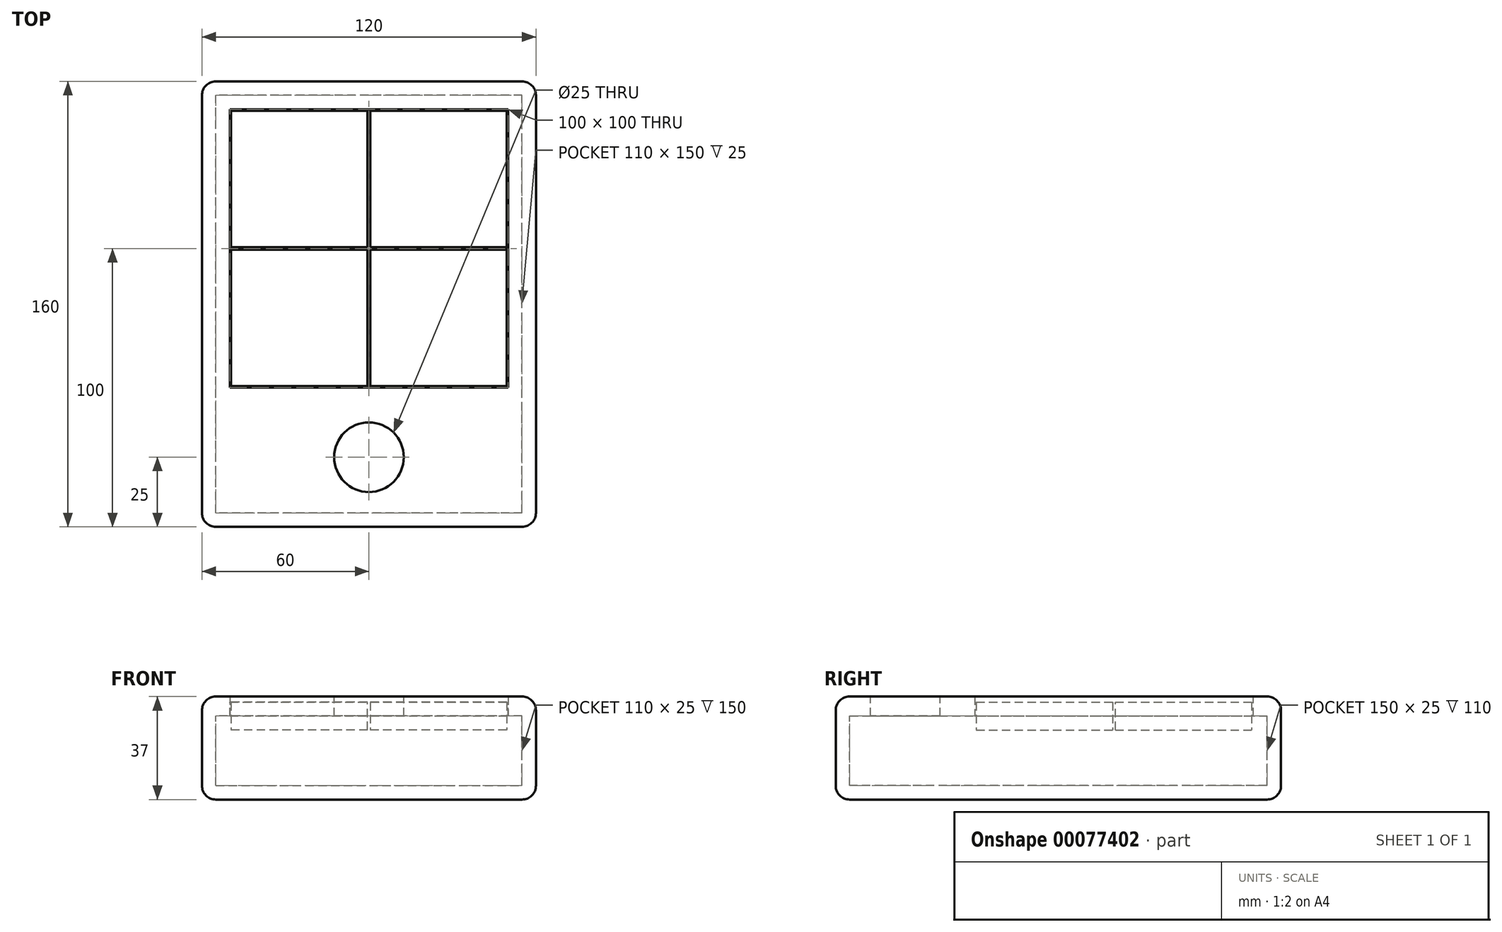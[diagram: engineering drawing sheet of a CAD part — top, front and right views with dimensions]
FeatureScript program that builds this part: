
annotation { "Feature Type Name" : "Feature", "Feature Type Description" : "" }
export const myFeature = defineFeature(function(context is Context, id is Id, definition is map)
    precondition{}
    {
        {
            var Q0;
            Q0=qCreatedBy(makeId("Top.planeOp"),FACE);
            var sketch = newSketch(context, id + "F0", { "sketchPlane" : qUnion([Q0])});
            skLineSegment(sketch, "E0.bottom", {"start": v(-50, 50) * mm, "end": v(50, 50) * mm});
            skLineSegment(sketch, "E0.top", {"start": v(-50, -50) * mm, "end": v(50, -50) * mm});
            skLineSegment(sketch, "E0.left", {"start": v(-50, 50) * mm, "end": v(-50, -50) * mm});
            skLineSegment(sketch, "E0.right", {"start": v(50, 50) * mm, "end": v(50, -50) * mm});
            skPoint(sketch, "E0.middle", {"position": v(0, 0) * mm});
            skSolve(sketch);
        }
        {
            var Q0;
            Q0=makeQuery(id+"F0.imprint","IMPRINT",FACE,{"disambiguationData":[TD([[makeQuery(id+"F0.imprint","IMPRINT",EDGE,{"derivedFrom":sQuery(id+"F0.wireOp",EDGE,"E0.bottom")}),-1.0]])]});
            extrude(context, id + "F1", {"entities" : qUnion([Q0]), "depth" : 10 * mm});
        }
        {
            var Q0;
            Q0=makeQuery(id+"F1.opExtrude","SWEPT_FACE",FACE,{"disambiguationData":[OSD([sQuery(id+"F0.wireOp",EDGE,"E0.top")])]});
            var sketch = newSketch(context, id + "F2", { "sketchPlane" : qUnion([Q0])});
            skLineSegment(sketch, "E1.bottom", {"start": v(-50, 10) * mm, "end": v(50, 10) * mm});
            skLineSegment(sketch, "E1.top", {"start": v(-50, 5) * mm, "end": v(50, 5) * mm});
            skLineSegment(sketch, "E1.left", {"start": v(-50, 10) * mm, "end": v(-50, 5) * mm});
            skLineSegment(sketch, "E1.right", {"start": v(50, 10) * mm, "end": v(50, 5) * mm});
            skSolve(sketch);
        }
        {
            var Q0;
            Q0=makeQuery(id+"F2.imprint","IMPRINT",FACE,{"disambiguationData":[TD([[makeQuery(id+"F2.imprint","IMPRINT",EDGE,{"derivedFrom":sQuery(id+"F2.wireOp",EDGE,"E1.bottom")}),-1.0]])]});
            extrude(context, id + "F3", {"entities" : qUnion([Q0]), "operationType" : NewBodyOperationType.ADD, "depth" : 50 * mm});
        }
        {
            var Q0;
            Q0=makeQuery(id+"F3.boolean.opBoolean","MERGE",FACE,{"derivedFrom":[makeQuery(id+"F1.opExtrude","CAP_FACE",FACE,{"disambiguationData":[OSD([sQuery(id+"F0.wireOp",EDGE,"E0.bottom"),sQuery(id+"F0.wireOp",EDGE,"E0.top"),sQuery(id+"F0.wireOp",EDGE,"E0.left"),sQuery(id+"F0.wireOp",EDGE,"E0.right")])],"isStart":false}),makeQuery(id+"F3.opExtrude","SWEPT_FACE",FACE,{"disambiguationData":[OSD([sQuery(id+"F2.wireOp",EDGE,"E1.bottom")])]})]});
            var sketch = newSketch(context, id + "F4", { "sketchPlane" : qUnion([Q0])});
            skLineSegment(sketch, "E2.bottom", {"start": v(-50, -100) * mm, "end": v(50, -100) * mm});
            skLineSegment(sketch, "E2.top", {"start": v(-50, -50) * mm, "end": v(50, -50) * mm});
            skLineSegment(sketch, "E2.left", {"start": v(-50, -100) * mm, "end": v(-50, -50) * mm});
            skLineSegment(sketch, "E2.right", {"start": v(50, -100) * mm, "end": v(50, -50) * mm});
            skSolve(sketch);
        }
        {
            var Q0;
            Q0=makeQuery(id+"F4.imprint","IMPRINT",FACE,{"disambiguationData":[TD([[makeQuery(id+"F4.imprint","IMPRINT",EDGE,{"derivedFrom":sQuery(id+"F4.wireOp",EDGE,"E2.bottom")}),1.0]])]});
            extrude(context, id + "F5", {"entities" : qUnion([Q0]), "operationType" : NewBodyOperationType.ADD, "depth" : 2 * mm});
        }
        {
            var Q0;
            Q0=makeQuery(id+"F5.boolean.opBoolean","MERGE",FACE,{"derivedFrom":[makeQuery(id+"F3.boolean.opBoolean","MERGE",FACE,{"derivedFrom":[makeQuery(id+"F1.opExtrude","SWEPT_FACE",FACE,{"disambiguationData":[OSD([sQuery(id+"F0.wireOp",EDGE,"E0.right")])]}),makeQuery(id+"F3.opExtrude","SWEPT_FACE",FACE,{"disambiguationData":[OSD([sQuery(id+"F2.wireOp",EDGE,"E1.right")])]})]}),makeQuery(id+"F5.opExtrude","SWEPT_FACE",FACE,{"disambiguationData":[OSD([sQuery(id+"F4.wireOp",EDGE,"E2.right")])]})]});
            var sketch = newSketch(context, id + "F6", { "sketchPlane" : qUnion([Q0])});
            skLineSegment(sketch, "E3", {"start": v(-50, 5) * mm, "end": v(50, 5) * mm});
            skSolve(sketch);
        }
        {
            var Q0;
            {var subQ4=sQuery(id+"F6.wireOp",EDGE,"E3");Q0=makeQuery(id+"F6.imprint","IMPRINT",FACE,{"disambiguationData":[TD([[makeQuery(id+"F6.imprint","IMPRINT",EDGE,{"derivedFrom":subQ4}),1.0]])]});}
            extrude(context, id + "F7", {"entities" : qUnion([Q0]), "operationType" : NewBodyOperationType.ADD, "depth" : 10 * mm});
        }
        {
            var Q0;
            {var subQ0=sQuery(id+"F2.wireOp",EDGE,"E1.bottom");var subQ1=sQuery(id+"F0.wireOp",EDGE,"E0.right");Q0=makeQuery(id+"F7.boolean.opBoolean","MERGE",FACE,{"derivedFrom":[makeQuery(id+"F3.boolean.opBoolean","MERGE",FACE,{"derivedFrom":[makeQuery(id+"F1.opExtrude","CAP_FACE",FACE,{"disambiguationData":[OSD([sQuery(id+"F0.wireOp",EDGE,"E0.bottom"),sQuery(id+"F0.wireOp",EDGE,"E0.top"),sQuery(id+"F0.wireOp",EDGE,"E0.left"),subQ1])],"isStart":false}),makeQuery(id+"F3.opExtrude","SWEPT_FACE",FACE,{"disambiguationData":[OSD([subQ0])]})]}),makeQuery(id+"F7.opExtrude","SWEPT_FACE",FACE,{"disambiguationData":[OSD([subQ1,subQ0,sQuery(id+"F2.wireOp",EDGE,"E1.right")])]})]});}
            var sketch = newSketch(context, id + "F8", { "sketchPlane" : qUnion([Q0])});
            skLineSegment(sketch, "E4.bottom", {"start": v(60, 50) * mm, "end": v(50, 50) * mm});
            skLineSegment(sketch, "E4.top", {"start": v(60, -50) * mm, "end": v(50, -50) * mm});
            skLineSegment(sketch, "E4.left", {"start": v(60, 50) * mm, "end": v(60, -50) * mm});
            skLineSegment(sketch, "E4.right", {"start": v(50, 50) * mm, "end": v(50, -50) * mm});
            skSolve(sketch);
        }
        {
            var Q0;
            Q0=makeQuery(id+"F8.imprint","IMPRINT",FACE,{"disambiguationData":[TD([[makeQuery(id+"F8.imprint","IMPRINT",EDGE,{"derivedFrom":sQuery(id+"F8.wireOp",EDGE,"E4.bottom")}),-1.0]])]});
            extrude(context, id + "F9", {"entities" : qUnion([Q0]), "operationType" : NewBodyOperationType.ADD, "depth" : 2 * mm});
        }
        {
            var Q0;
            {var subQ0=sQuery(id+"F0.wireOp",EDGE,"E0.bottom");Q0=makeQuery(id+"F9.boolean.opBoolean","MERGE",FACE,{"derivedFrom":[makeQuery(id+"F7.boolean.opBoolean","MERGE",FACE,{"derivedFrom":[makeQuery(id+"F1.opExtrude","SWEPT_FACE",FACE,{"disambiguationData":[OSD([subQ0])]}),makeQuery(id+"F7.opExtrude","SWEPT_FACE",FACE,{"disambiguationData":[OSD([subQ0,sQuery(id+"F0.wireOp",EDGE,"E0.right")])]})]}),makeQuery(id+"F9.opExtrude","SWEPT_FACE",FACE,{"disambiguationData":[OSD([sQuery(id+"F8.wireOp",EDGE,"E4.bottom")])]})]});}
            var sketch = newSketch(context, id + "F10", { "sketchPlane" : qUnion([Q0])});
            skLineSegment(sketch, "E5", {"start": v(-50, 5) * mm, "end": v(50, 5) * mm});
            skSolve(sketch);
        }
        {
            var Q0;
            {var subQ5=sQuery(id+"F10.wireOp",EDGE,"E5");Q0=makeQuery(id+"F10.imprint","IMPRINT",FACE,{"disambiguationData":[TD([[makeQuery(id+"F10.imprint","IMPRINT",EDGE,{"derivedFrom":subQ5}),1.0]])]});}
            extrude(context, id + "F11", {"entities" : qUnion([Q0]), "operationType" : NewBodyOperationType.ADD, "depth" : 10 * mm});
        }
        {
            var Q0;
            {var subQ0=sQuery(id+"F2.wireOp",EDGE,"E1.right");var subQ1=sQuery(id+"F2.wireOp",EDGE,"E1.bottom");var subQ2=sQuery(id+"F0.wireOp",EDGE,"E0.right");var subQ3=sQuery(id+"F0.wireOp",EDGE,"E0.bottom");Q0=makeQuery(id+"F11.boolean.opBoolean","MERGE",FACE,{"derivedFrom":[makeQuery(id+"F7.boolean.opBoolean","MERGE",FACE,{"derivedFrom":[makeQuery(id+"F3.boolean.opBoolean","MERGE",FACE,{"derivedFrom":[makeQuery(id+"F1.opExtrude","CAP_FACE",FACE,{"disambiguationData":[OSD([subQ3,sQuery(id+"F0.wireOp",EDGE,"E0.top"),sQuery(id+"F0.wireOp",EDGE,"E0.left"),subQ2])],"isStart":false}),makeQuery(id+"F3.opExtrude","SWEPT_FACE",FACE,{"disambiguationData":[OSD([subQ1])]})]}),makeQuery(id+"F7.opExtrude","SWEPT_FACE",FACE,{"disambiguationData":[OSD([subQ2,subQ1,subQ0])]})]}),makeQuery(id+"F11.opExtrude","SWEPT_FACE",FACE,{"disambiguationData":[OSD([subQ3,subQ2,subQ1,subQ0])]})]});}
            var sketch = newSketch(context, id + "F12", { "sketchPlane" : qUnion([Q0])});
            skLineSegment(sketch, "E6.bottom", {"start": v(-50, 60) * mm, "end": v(50, 60) * mm});
            skLineSegment(sketch, "E6.top", {"start": v(-50, 49.98) * mm, "end": v(50, 49.98) * mm});
            skLineSegment(sketch, "E6.left", {"start": v(-50, 60) * mm, "end": v(-50, 49.98) * mm});
            skLineSegment(sketch, "E6.right", {"start": v(50, 60) * mm, "end": v(50, 49.98) * mm});
            skSolve(sketch);
        }
        {
            var Q0;
            Q0 = qSketchRegion(id + "F12", true);
            extrude(context, id + "F13", {"entities" : qUnion([Q0]), "operationType" : NewBodyOperationType.ADD, "depth" : 2 * mm});
        }
        {
            var Q0;
            {var subQ0=sQuery(id+"F0.wireOp",EDGE,"E0.left");Q0=makeQuery(id+"F13.boolean.opBoolean","MERGE",FACE,{"derivedFrom":[makeQuery(id+"F11.boolean.opBoolean","MERGE",FACE,{"derivedFrom":[makeQuery(id+"F5.boolean.opBoolean","MERGE",FACE,{"derivedFrom":[makeQuery(id+"F3.boolean.opBoolean","MERGE",FACE,{"derivedFrom":[makeQuery(id+"F1.opExtrude","SWEPT_FACE",FACE,{"disambiguationData":[OSD([subQ0])]}),makeQuery(id+"F3.opExtrude","SWEPT_FACE",FACE,{"disambiguationData":[OSD([sQuery(id+"F2.wireOp",EDGE,"E1.left")])]})]}),makeQuery(id+"F5.opExtrude","SWEPT_FACE",FACE,{"disambiguationData":[OSD([sQuery(id+"F4.wireOp",EDGE,"E2.left")])]})]}),makeQuery(id+"F11.opExtrude","SWEPT_FACE",FACE,{"disambiguationData":[OSD([sQuery(id+"F0.wireOp",EDGE,"E0.bottom"),subQ0])]})]}),makeQuery(id+"F13.opExtrude","SWEPT_FACE",FACE,{"disambiguationData":[OSD([sQuery(id+"F12.wireOp",EDGE,"E6.left")])]})]});}
            var sketch = newSketch(context, id + "F14", { "sketchPlane" : qUnion([Q0])});
            skSolve(sketch);
        }
        {
            var Q0;
            Q0 = qSketchRegion(id + "F14", true);
            var Q1;
            {var subQ5=sQuery(id+"F0.wireOp",EDGE,"E0.left");Q1=makeQuery(id+"F14.imprint","IMPRINT",FACE,{"disambiguationData":[TD([[makeQuery(id+"F14.imprint","IMPRINT",EDGE,{"derivedFrom":makeQuery(id+"F1.opExtrude","CAP_EDGE",EDGE,{"disambiguationData":[OSD([subQ5])],"isStart":true})}),1.0]])]});}
            extrude(context, id + "F15", {"entities" : qUnion([Q0, Q1]), "operationType" : NewBodyOperationType.ADD, "depth" : 10 * mm});
        }
        {
            var Q0;
            {var subQ0=sQuery(id+"F2.wireOp",EDGE,"E1.right");var subQ1=sQuery(id+"F2.wireOp",EDGE,"E1.bottom");var subQ2=sQuery(id+"F0.wireOp",EDGE,"E0.right");var subQ3=sQuery(id+"F0.wireOp",EDGE,"E0.left");var subQ4=sQuery(id+"F0.wireOp",EDGE,"E0.bottom");Q0=makeQuery(id+"F15.boolean.opBoolean","MERGE",FACE,{"derivedFrom":[makeQuery(id+"F11.boolean.opBoolean","MERGE",FACE,{"derivedFrom":[makeQuery(id+"F7.boolean.opBoolean","MERGE",FACE,{"derivedFrom":[makeQuery(id+"F3.boolean.opBoolean","MERGE",FACE,{"derivedFrom":[makeQuery(id+"F1.opExtrude","CAP_FACE",FACE,{"disambiguationData":[OSD([subQ4,sQuery(id+"F0.wireOp",EDGE,"E0.top"),subQ3,subQ2])],"isStart":false}),makeQuery(id+"F3.opExtrude","SWEPT_FACE",FACE,{"disambiguationData":[OSD([subQ1])]})]}),makeQuery(id+"F7.opExtrude","SWEPT_FACE",FACE,{"disambiguationData":[OSD([subQ2,subQ1,subQ0])]})]}),makeQuery(id+"F11.opExtrude","SWEPT_FACE",FACE,{"disambiguationData":[OSD([subQ4,subQ2,subQ1,subQ0])]})]}),makeQuery(id+"F15.opExtrude","SWEPT_FACE",FACE,{"disambiguationData":[OSD([subQ4,subQ3,subQ2,subQ1,sQuery(id+"F2.wireOp",EDGE,"E1.left"),subQ0])]})]});}
            var sketch = newSketch(context, id + "F16", { "sketchPlane" : qUnion([Q0])});
            skLineSegment(sketch, "E7.bottom", {"start": v(-60, 49.98) * mm, "end": v(-50, 49.98) * mm});
            skLineSegment(sketch, "E7.top", {"start": v(-60, -50) * mm, "end": v(-50, -50) * mm});
            skLineSegment(sketch, "E7.left", {"start": v(-60, 49.98) * mm, "end": v(-60, -50) * mm});
            skLineSegment(sketch, "E7.right", {"start": v(-50, 49.98) * mm, "end": v(-50, -50) * mm});
            skSolve(sketch);
        }
        {
            var Q0;
            Q0 = qSketchRegion(id + "F16", true);
            extrude(context, id + "F17", {"entities" : qUnion([Q0]), "operationType" : NewBodyOperationType.ADD, "depth" : 2 * mm});
        }
        {
            var Q0;
            {var subQ0=sQuery(id+"F2.wireOp",EDGE,"E1.right");var subQ1=sQuery(id+"F2.wireOp",EDGE,"E1.bottom");var subQ2=sQuery(id+"F0.wireOp",EDGE,"E0.right");var subQ3=sQuery(id+"F0.wireOp",EDGE,"E0.left");var subQ4=sQuery(id+"F0.wireOp",EDGE,"E0.bottom");Q0=makeQuery(id+"F15.boolean.opBoolean","MERGE",FACE,{"derivedFrom":[makeQuery(id+"F11.boolean.opBoolean","MERGE",FACE,{"derivedFrom":[makeQuery(id+"F7.boolean.opBoolean","MERGE",FACE,{"derivedFrom":[makeQuery(id+"F3.boolean.opBoolean","MERGE",FACE,{"derivedFrom":[makeQuery(id+"F1.opExtrude","CAP_FACE",FACE,{"disambiguationData":[OSD([subQ4,sQuery(id+"F0.wireOp",EDGE,"E0.top"),subQ3,subQ2])],"isStart":false}),makeQuery(id+"F3.opExtrude","SWEPT_FACE",FACE,{"disambiguationData":[OSD([subQ1])]})]}),makeQuery(id+"F7.opExtrude","SWEPT_FACE",FACE,{"disambiguationData":[OSD([subQ2,subQ1,subQ0])]})]}),makeQuery(id+"F11.opExtrude","SWEPT_FACE",FACE,{"disambiguationData":[OSD([subQ4,subQ2,subQ1,subQ0])]})]}),makeQuery(id+"F15.opExtrude","SWEPT_FACE",FACE,{"disambiguationData":[OSD([subQ4,subQ3,subQ2,subQ1,sQuery(id+"F2.wireOp",EDGE,"E1.left"),subQ0])]})]});}
            var sketch = newSketch(context, id + "F18", { "sketchPlane" : qUnion([Q0])});
            skLineSegment(sketch, "E8.bottom", {"start": v(0.5, -50) * mm, "end": v(-0.5, -50) * mm});
            skLineSegment(sketch, "E8.left", {"start": v(0.5, -50) * mm, "end": v(0.5, -0.5) * mm});
            skLineSegment(sketch, "E8.right", {"start": v(-0.5, -50) * mm, "end": v(-0.5, -0.5) * mm});
            skLineSegment(sketch, "E9.bottom", {"start": v(-0.5, -0.5) * mm, "end": v(-50, -0.5) * mm});
            skLineSegment(sketch, "E9.top", {"start": v(-0.5, 0.48) * mm, "end": v(-50, 0.48) * mm});
            skLineSegment(sketch, "E9.right", {"start": v(-50, -0.5) * mm, "end": v(-50, 0.48) * mm});
            skLineSegment(sketch, "E10.top", {"start": v(0.5, 49.98) * mm, "end": v(-0.5, 49.98) * mm});
            skLineSegment(sketch, "E10.left", {"start": v(0.5, 0.48) * mm, "end": v(0.5, 49.98) * mm});
            skLineSegment(sketch, "E10.right", {"start": v(-0.5, 0.48) * mm, "end": v(-0.5, 49.98) * mm});
            skLineSegment(sketch, "E11.bottom", {"start": v(50, -0.5) * mm, "end": v(0.5, -0.5) * mm});
            skLineSegment(sketch, "E11.top", {"start": v(50, 0.48) * mm, "end": v(0.5, 0.48) * mm});
            skLineSegment(sketch, "E11.left", {"start": v(50, -0.5) * mm, "end": v(50, 0.48) * mm});
            skSolve(sketch);
        }
        {
            var Q0;
            Q0 = qSketchRegion(id + "F18", true);
            extrude(context, id + "F19", {"entities" : qUnion([Q0]), "operationType" : NewBodyOperationType.REMOVE, "oppositeDirection" : true, "depth" : 10 * mm});
        }
        {
            var Q0;
            {var subQ0=sQuery(id+"F0.wireOp",EDGE,"E0.left");Q0=makeQuery(id+"F15.boolean.opBoolean","MERGE",FACE,{"derivedFrom":[makeQuery(id+"F1.opExtrude","CAP_FACE",FACE,{"disambiguationData":[OSD([sQuery(id+"F0.wireOp",EDGE,"E0.bottom"),sQuery(id+"F0.wireOp",EDGE,"E0.top"),subQ0,sQuery(id+"F0.wireOp",EDGE,"E0.right")])],"isStart":true}),makeQuery(id+"F15.opExtrude","SWEPT_FACE",FACE,{"disambiguationData":[OSD([subQ0])]})]});}
            var sketch = newSketch(context, id + "F20", { "sketchPlane" : qUnion([Q0])});
            skLineSegment(sketch, "E12.bottom", {"start": v(-60, 50) * mm, "end": v(-50, 50) * mm});
            skLineSegment(sketch, "E12.top", {"start": v(-60, -50) * mm, "end": v(-50, -50) * mm});
            skLineSegment(sketch, "E12.left", {"start": v(-60, 50) * mm, "end": v(-60, -50) * mm});
            skLineSegment(sketch, "E12.right", {"start": v(-50, 50) * mm, "end": v(-50, -50) * mm});
            skSolve(sketch);
        }
        {
            var Q0;
            Q0 = qSketchRegion(id + "F20", true);
            extrude(context, id + "F21", {"entities" : qUnion([Q0]), "operationType" : NewBodyOperationType.REMOVE, "oppositeDirection" : true, "depth" : 5 * mm});
        }
        {
            var Q0;
            {var subQ0=sQuery(id+"F12.wireOp",EDGE,"E6.left");var subQ1=sQuery(id+"F4.wireOp",EDGE,"E2.left");var subQ2=sQuery(id+"F8.wireOp",EDGE,"E4.bottom");var subQ3=sQuery(id+"F4.wireOp",EDGE,"E2.right");Q0=makeQuery(id+"F17.boolean.opBoolean","MERGE",FACE,{"derivedFrom":[makeQuery(id+"F15.boolean.opBoolean","MERGE",FACE,{"derivedFrom":[makeQuery(id+"F13.boolean.opBoolean","MERGE",FACE,{"derivedFrom":[makeQuery(id+"F11.boolean.opBoolean","MERGE",FACE,{"derivedFrom":[makeQuery(id+"F9.boolean.opBoolean","MERGE",FACE,{"derivedFrom":[makeQuery(id+"F7.boolean.opBoolean","MERGE",FACE,{"derivedFrom":[makeQuery(id+"F5.opExtrude","CAP_FACE",FACE,{"disambiguationData":[OSD([sQuery(id+"F4.wireOp",EDGE,"E2.bottom"),sQuery(id+"F4.wireOp",EDGE,"E2.top"),subQ1,subQ3])],"isStart":false}),makeQuery(id+"F7.opExtrude","SWEPT_FACE",FACE,{"disambiguationData":[OSD([subQ3])]})]}),makeQuery(id+"F9.opExtrude","CAP_FACE",FACE,{"disambiguationData":[OSD([subQ2,sQuery(id+"F8.wireOp",EDGE,"E4.top"),sQuery(id+"F8.wireOp",EDGE,"E4.left"),sQuery(id+"F8.wireOp",EDGE,"E4.right")])],"isStart":false})]}),makeQuery(id+"F11.opExtrude","SWEPT_FACE",FACE,{"disambiguationData":[OSD([subQ2])]})]}),makeQuery(id+"F13.opExtrude","CAP_FACE",FACE,{"disambiguationData":[OSD([sQuery(id+"F12.wireOp",EDGE,"E6.bottom"),sQuery(id+"F12.wireOp",EDGE,"E6.top"),subQ0,sQuery(id+"F12.wireOp",EDGE,"E6.right")])],"isStart":false})]}),makeQuery(id+"F15.opExtrude","SWEPT_FACE",FACE,{"disambiguationData":[OSD([subQ1])]}),makeQuery(id+"F15.opExtrude","SWEPT_FACE",FACE,{"disambiguationData":[OSD([subQ0])]})]}),makeQuery(id+"F17.opExtrude","CAP_FACE",FACE,{"disambiguationData":[OSD([sQuery(id+"F16.wireOp",EDGE,"E7.bottom"),sQuery(id+"F16.wireOp",EDGE,"E7.top"),sQuery(id+"F16.wireOp",EDGE,"E7.left"),sQuery(id+"F16.wireOp",EDGE,"E7.right")])],"isStart":false})]});}
            var sketch = newSketch(context, id + "F22", { "sketchPlane" : qUnion([Q0])});
            skCircle(sketch, "E13", {"center": v(0, -75) * mm, "radius": 12.5 * mm});
            skSolve(sketch);
        }
        {
            var Q0;
            Q0 = qSketchRegion(id + "F22", true);
            extrude(context, id + "F23", {"entities" : qUnion([Q0]), "operationType" : NewBodyOperationType.REMOVE, "oppositeDirection" : true, "depth" : 7 * mm});
        }
        {
            var Q0;
            {var subQ1=sQuery(id+"F2.wireOp",EDGE,"E1.left");var subQ2=sQuery(id+"F2.wireOp",EDGE,"E1.bottom");var subQ3=sQuery(id+"F0.wireOp",EDGE,"E0.left");var subQ4=sQuery(id+"F2.wireOp",EDGE,"E1.right");var subQ5=sQuery(id+"F0.wireOp",EDGE,"E0.right");var subQ6=sQuery(id+"F0.wireOp",EDGE,"E0.bottom");Q0=makeQuery(id+"F19.boolean.opBoolean","SPLIT",FACE,{"disambiguationData":[TD([makeQuery(id+"F19.opExtrude","SWEPT_FACE",FACE,{"disambiguationData":[OSD([sQuery(id+"F18.wireOp",EDGE,"E8.right")])]})])],"derivedFrom":makeQuery(id+"F15.boolean.opBoolean","MERGE",FACE,{"derivedFrom":[makeQuery(id+"F11.boolean.opBoolean","MERGE",FACE,{"derivedFrom":[makeQuery(id+"F7.boolean.opBoolean","MERGE",FACE,{"derivedFrom":[makeQuery(id+"F3.boolean.opBoolean","MERGE",FACE,{"derivedFrom":[makeQuery(id+"F1.opExtrude","CAP_FACE",FACE,{"disambiguationData":[OSD([subQ6,sQuery(id+"F0.wireOp",EDGE,"E0.top"),subQ3,subQ5])],"isStart":false}),makeQuery(id+"F3.opExtrude","SWEPT_FACE",FACE,{"disambiguationData":[OSD([subQ2])]})]}),makeQuery(id+"F7.opExtrude","SWEPT_FACE",FACE,{"disambiguationData":[OSD([subQ5,subQ2,subQ4])]})]}),makeQuery(id+"F11.opExtrude","SWEPT_FACE",FACE,{"disambiguationData":[OSD([subQ6,subQ5,subQ2,subQ4])]})]}),makeQuery(id+"F15.opExtrude","SWEPT_FACE",FACE,{"disambiguationData":[OSD([subQ6,subQ3,subQ5,subQ2,subQ1,subQ4])]})]})});}
            var sketch = newSketch(context, id + "F24", { "sketchPlane" : qUnion([Q0])});
            skLineSegment(sketch, "E14.bottom", {"start": v(-49.5, -49.5) * mm, "end": v(49.5, -49.5) * mm});
            skLineSegment(sketch, "E14.top", {"start": v(-49.5, 49.48) * mm, "end": v(49.5, 49.48) * mm});
            skLineSegment(sketch, "E14.left", {"start": v(-49.5, -49.5) * mm, "end": v(-49.5, 49.48) * mm});
            skLineSegment(sketch, "E14.right", {"start": v(49.5, -49.5) * mm, "end": v(49.5, 49.48) * mm});
            skLineSegment(sketch, "E15.bottom", {"start": v(50, -50) * mm, "end": v(-50, -50) * mm});
            skLineSegment(sketch, "E15.top", {"start": v(50, 50) * mm, "end": v(-50, 50) * mm});
            skLineSegment(sketch, "E15.left", {"start": v(50, -50) * mm, "end": v(50, 50) * mm});
            skLineSegment(sketch, "E15.right", {"start": v(-50, -50) * mm, "end": v(-50, 50) * mm});
            skSolve(sketch);
        }
        {
            var Q0;
            Q0 = qSketchRegion(id + "F24", true);
            extrude(context, id + "F25", {"entities" : qUnion([Q0]), "operationType" : NewBodyOperationType.REMOVE, "oppositeDirection" : true, "depth" : 10 * mm});
        }
        {
            var Q0;
            {var subQ0=sQuery(id+"F10.wireOp",EDGE,"E5");var subQ1=sQuery(id+"F0.wireOp",EDGE,"E0.left");var subQ2=sQuery(id+"F0.wireOp",EDGE,"E0.bottom");var subQ3=sQuery(id+"F2.wireOp",EDGE,"E1.top");var subQ4=sQuery(id+"F0.wireOp",EDGE,"E0.top");var subQ5=sQuery(id+"F6.wireOp",EDGE,"E3");var subQ6=sQuery(id+"F0.wireOp",EDGE,"E0.right");Q0=makeQuery(id+"F21.boolean.opBoolean","MERGE",FACE,{"derivedFrom":[makeQuery(id+"F15.boolean.opBoolean","MERGE",FACE,{"derivedFrom":[makeQuery(id+"F11.boolean.opBoolean","MERGE",FACE,{"derivedFrom":[makeQuery(id+"F7.boolean.opBoolean","MERGE",FACE,{"derivedFrom":[makeQuery(id+"F3.opExtrude","SWEPT_FACE",FACE,{"disambiguationData":[OSD([subQ3])]}),makeQuery(id+"F7.opExtrude","SWEPT_FACE",FACE,{"disambiguationData":[OSD([subQ4,subQ6,subQ3,sQuery(id+"F2.wireOp",EDGE,"E1.right"),subQ5])]})]}),makeQuery(id+"F11.opExtrude","SWEPT_FACE",FACE,{"disambiguationData":[OSD([subQ2,subQ6,subQ5,subQ0])]})]}),makeQuery(id+"F15.opExtrude","SWEPT_FACE",FACE,{"disambiguationData":[OSD([subQ4,subQ1,subQ3,sQuery(id+"F2.wireOp",EDGE,"E1.left")])]}),makeQuery(id+"F15.opExtrude","SWEPT_FACE",FACE,{"disambiguationData":[OSD([subQ2,subQ1,subQ0])]})]}),makeQuery(id+"F21.opExtrude","CAP_FACE",FACE,{"disambiguationData":[OSD([sQuery(id+"F20.wireOp",EDGE,"E12.bottom"),sQuery(id+"F20.wireOp",EDGE,"E12.top"),sQuery(id+"F20.wireOp",EDGE,"E12.left"),sQuery(id+"F20.wireOp",EDGE,"E12.right")])],"isStart":false})]});}
            var sketch = newSketch(context, id + "F26", { "sketchPlane" : qUnion([Q0])});
            skLineSegment(sketch, "E16.bottom", {"start": v(55, 95) * mm, "end": v(-55, 95) * mm});
            skLineSegment(sketch, "E16.top", {"start": v(55, -55) * mm, "end": v(-55, -55) * mm});
            skLineSegment(sketch, "E16.left", {"start": v(55, 95) * mm, "end": v(55, -55) * mm});
            skLineSegment(sketch, "E16.right", {"start": v(-55, 95) * mm, "end": v(-55, -55) * mm});
            skSolve(sketch);
        }
        {
            var Q0;
            Q0=makeQuery(id+"F26.imprint","IMPRINT",FACE,{"disambiguationData":[TD([[makeQuery(id+"F26.imprint","IMPRINT",EDGE,{"derivedFrom":sQuery(id+"F26.wireOp",EDGE,"E16.bottom")}),-1.0]])]});
            extrude(context, id + "F27", {"entities" : qUnion([Q0]), "operationType" : NewBodyOperationType.ADD, "depth" : 30 * mm});
        }
        {
            var Q0;
            Q0=makeQuery(id+"F27.opExtrude","SWEPT_FACE",FACE,{"disambiguationData":[OSD([sQuery(id+"F26.wireOp",EDGE,"E16.left")])]});
            var sketch = newSketch(context, id + "F28", { "sketchPlane" : qUnion([Q0])});
            skLineSegment(sketch, "E17.bottom", {"start": v(-55, -25) * mm, "end": v(95, -25) * mm});
            skLineSegment(sketch, "E17.top", {"start": v(-55, -20) * mm, "end": v(95, -20) * mm});
            skLineSegment(sketch, "E17.left", {"start": v(-55, -25) * mm, "end": v(-55, -20) * mm});
            skLineSegment(sketch, "E17.right", {"start": v(95, -25) * mm, "end": v(95, -20) * mm});
            skSolve(sketch);
        }
        {
            var Q0;
            Q0 = qSketchRegion(id + "F28", true);
            extrude(context, id + "F29", {"entities" : qUnion([Q0]), "operationType" : NewBodyOperationType.ADD, "depth" : 110 * mm});
        }
        {
            var Q0;
            {var subQ0=sQuery(id+"F8.wireOp",EDGE,"E4.left");Q0=makeQuery(id+"F11.boolean.opBoolean","MERGE",EDGE,{"derivedFrom":[makeQuery(id+"F9.boolean.opBoolean","MERGE",EDGE,{"derivedFrom":[makeQuery(id+"F7.opExtrude","CAP_EDGE",EDGE,{"disambiguationData":[OSD([sQuery(id+"F4.wireOp",EDGE,"E2.right")])],"isStart":false}),makeQuery(id+"F9.opExtrude","CAP_EDGE",EDGE,{"disambiguationData":[OSD([subQ0])],"isStart":false})]}),makeQuery(id+"F11.opExtrude","SWEPT_EDGE",EDGE,{"disambiguationData":[OSD([sQuery(id+"F0.wireOp",EDGE,"E0.bottom"),sQuery(id+"F0.wireOp",EDGE,"E0.right"),sQuery(id+"F8.wireOp",EDGE,"E4.bottom"),subQ0])]})]});}
            var Q1;
            Q1=makeQuery(id+"F27.opExtrude","CAP_EDGE",EDGE,{"disambiguationData":[OSD([sQuery(id+"F0.wireOp",EDGE,"E0.bottom"),sQuery(id+"F0.wireOp",EDGE,"E0.top"),sQuery(id+"F0.wireOp",EDGE,"E0.right"),sQuery(id+"F2.wireOp",EDGE,"E1.top"),sQuery(id+"F2.wireOp",EDGE,"E1.right"),sQuery(id+"F6.wireOp",EDGE,"E3"),sQuery(id+"F8.wireOp",EDGE,"E4.bottom"),sQuery(id+"F8.wireOp",EDGE,"E4.left")])],"isStart":false});
            var Q2;
            {var subQ0=sQuery(id+"F4.wireOp",EDGE,"E2.right");var subQ1=sQuery(id+"F4.wireOp",EDGE,"E2.bottom");var subQ2=sQuery(id+"F2.wireOp",EDGE,"E1.right");Q2=makeQuery(id+"F27.boolean.opBoolean","MERGE",EDGE,{"derivedFrom":[makeQuery(id+"F7.opExtrude","CAP_EDGE",EDGE,{"disambiguationData":[OSD([subQ2,subQ1,subQ0])],"isStart":false}),makeQuery(id+"F27.opExtrude","SWEPT_EDGE",EDGE,{"disambiguationData":[OSD([sQuery(id+"F0.wireOp",EDGE,"E0.bottom"),sQuery(id+"F0.wireOp",EDGE,"E0.top"),sQuery(id+"F0.wireOp",EDGE,"E0.left"),sQuery(id+"F0.wireOp",EDGE,"E0.right"),sQuery(id+"F2.wireOp",EDGE,"E1.top"),sQuery(id+"F2.wireOp",EDGE,"E1.left"),subQ2,subQ1,sQuery(id+"F4.wireOp",EDGE,"E2.left"),subQ0,sQuery(id+"F6.wireOp",EDGE,"E3"),sQuery(id+"F8.wireOp",EDGE,"E4.bottom"),sQuery(id+"F8.wireOp",EDGE,"E4.left")])]})]});}
            var Q3;
            {var subQ0=sQuery(id+"F4.wireOp",EDGE,"E2.bottom");Q3=makeQuery(id+"F15.boolean.opBoolean","MERGE",EDGE,{"derivedFrom":[makeQuery(id+"F7.boolean.opBoolean","MERGE",EDGE,{"derivedFrom":[makeQuery(id+"F5.opExtrude","CAP_EDGE",EDGE,{"disambiguationData":[OSD([subQ0])],"isStart":false}),makeQuery(id+"F7.opExtrude","SWEPT_EDGE",EDGE,{"disambiguationData":[OSD([sQuery(id+"F2.wireOp",EDGE,"E1.right"),subQ0,sQuery(id+"F4.wireOp",EDGE,"E2.right")])]})]}),makeQuery(id+"F15.opExtrude","SWEPT_EDGE",EDGE,{"disambiguationData":[OSD([sQuery(id+"F2.wireOp",EDGE,"E1.left"),subQ0,sQuery(id+"F4.wireOp",EDGE,"E2.left")])]})]});}
            var Q4;
            Q4=makeQuery(id+"F27.opExtrude","CAP_EDGE",EDGE,{"disambiguationData":[OSD([sQuery(id+"F0.wireOp",EDGE,"E0.top"),sQuery(id+"F0.wireOp",EDGE,"E0.left"),sQuery(id+"F0.wireOp",EDGE,"E0.right"),sQuery(id+"F2.wireOp",EDGE,"E1.top"),sQuery(id+"F2.wireOp",EDGE,"E1.left"),sQuery(id+"F2.wireOp",EDGE,"E1.right"),sQuery(id+"F4.wireOp",EDGE,"E2.bottom"),sQuery(id+"F4.wireOp",EDGE,"E2.left"),sQuery(id+"F4.wireOp",EDGE,"E2.right")])],"isStart":false});
            var Q5;
            Q5=makeQuery(id+"F27.opExtrude","CAP_EDGE",EDGE,{"disambiguationData":[OSD([sQuery(id+"F0.wireOp",EDGE,"E0.bottom"),sQuery(id+"F0.wireOp",EDGE,"E0.top"),sQuery(id+"F0.wireOp",EDGE,"E0.left"),sQuery(id+"F2.wireOp",EDGE,"E1.top"),sQuery(id+"F2.wireOp",EDGE,"E1.left"),sQuery(id+"F10.wireOp",EDGE,"E5"),sQuery(id+"F20.wireOp",EDGE,"E12.left")])],"isStart":false});
            var Q6;
            {var subQ0=sQuery(id+"F4.wireOp",EDGE,"E2.left");var subQ1=sQuery(id+"F4.wireOp",EDGE,"E2.bottom");var subQ2=sQuery(id+"F2.wireOp",EDGE,"E1.left");Q6=makeQuery(id+"F27.boolean.opBoolean","MERGE",EDGE,{"derivedFrom":[makeQuery(id+"F15.opExtrude","CAP_EDGE",EDGE,{"disambiguationData":[OSD([subQ2,subQ1,subQ0])],"isStart":false}),makeQuery(id+"F27.opExtrude","SWEPT_EDGE",EDGE,{"disambiguationData":[OSD([sQuery(id+"F0.wireOp",EDGE,"E0.bottom"),sQuery(id+"F0.wireOp",EDGE,"E0.top"),sQuery(id+"F0.wireOp",EDGE,"E0.left"),sQuery(id+"F0.wireOp",EDGE,"E0.right"),sQuery(id+"F2.wireOp",EDGE,"E1.top"),subQ2,sQuery(id+"F2.wireOp",EDGE,"E1.right"),subQ1,subQ0,sQuery(id+"F4.wireOp",EDGE,"E2.right"),sQuery(id+"F10.wireOp",EDGE,"E5"),sQuery(id+"F20.wireOp",EDGE,"E12.left")])]})]});}
            var Q7;
            Q7=makeQuery(id+"F17.boolean.opBoolean","MERGE",EDGE,{"derivedFrom":[makeQuery(id+"F15.opExtrude","CAP_EDGE",EDGE,{"disambiguationData":[OSD([sQuery(id+"F4.wireOp",EDGE,"E2.left")])],"isStart":false}),makeQuery(id+"F15.opExtrude","CAP_EDGE",EDGE,{"disambiguationData":[OSD([sQuery(id+"F12.wireOp",EDGE,"E6.left")])],"isStart":false}),makeQuery(id+"F17.opExtrude","CAP_EDGE",EDGE,{"disambiguationData":[OSD([sQuery(id+"F16.wireOp",EDGE,"E7.left")])],"isStart":false})]});
            var Q8;
            {var subQ0=sQuery(id+"F12.wireOp",EDGE,"E6.left");var subQ1=sQuery(id+"F12.wireOp",EDGE,"E6.bottom");var subQ2=sQuery(id+"F0.wireOp",EDGE,"E0.left");var subQ3=sQuery(id+"F0.wireOp",EDGE,"E0.bottom");Q8=makeQuery(id+"F27.boolean.opBoolean","MERGE",EDGE,{"derivedFrom":[makeQuery(id+"F15.opExtrude","CAP_EDGE",EDGE,{"disambiguationData":[OSD([subQ3,subQ2,subQ1,subQ0])],"isStart":false}),makeQuery(id+"F27.opExtrude","SWEPT_EDGE",EDGE,{"disambiguationData":[OSD([subQ3,sQuery(id+"F0.wireOp",EDGE,"E0.top"),subQ2,sQuery(id+"F0.wireOp",EDGE,"E0.right"),sQuery(id+"F2.wireOp",EDGE,"E1.top"),sQuery(id+"F2.wireOp",EDGE,"E1.left"),sQuery(id+"F6.wireOp",EDGE,"E3"),sQuery(id+"F10.wireOp",EDGE,"E5"),subQ1,subQ0,sQuery(id+"F20.wireOp",EDGE,"E12.left")])]})]});}
            var Q9;
            {var subQ0=sQuery(id+"F12.wireOp",EDGE,"E6.bottom");Q9=makeQuery(id+"F15.boolean.opBoolean","MERGE",EDGE,{"derivedFrom":[makeQuery(id+"F13.boolean.opBoolean","MERGE",EDGE,{"derivedFrom":[makeQuery(id+"F11.opExtrude","CAP_EDGE",EDGE,{"disambiguationData":[OSD([sQuery(id+"F8.wireOp",EDGE,"E4.bottom")])],"isStart":false}),makeQuery(id+"F13.opExtrude","CAP_EDGE",EDGE,{"disambiguationData":[OSD([subQ0])],"isStart":false})]}),makeQuery(id+"F15.opExtrude","SWEPT_EDGE",EDGE,{"disambiguationData":[OSD([sQuery(id+"F0.wireOp",EDGE,"E0.bottom"),sQuery(id+"F0.wireOp",EDGE,"E0.left"),subQ0,sQuery(id+"F12.wireOp",EDGE,"E6.left")])]})]});}
            var Q10;
            Q10=makeQuery(id+"F27.opExtrude","CAP_EDGE",EDGE,{"disambiguationData":[OSD([sQuery(id+"F0.wireOp",EDGE,"E0.bottom"),sQuery(id+"F0.wireOp",EDGE,"E0.left"),sQuery(id+"F0.wireOp",EDGE,"E0.right"),sQuery(id+"F6.wireOp",EDGE,"E3"),sQuery(id+"F10.wireOp",EDGE,"E5"),sQuery(id+"F12.wireOp",EDGE,"E6.bottom"),sQuery(id+"F12.wireOp",EDGE,"E6.left")])],"isStart":false});
            var Q11;
            {var subQ0=sQuery(id+"F8.wireOp",EDGE,"E4.left");var subQ1=sQuery(id+"F8.wireOp",EDGE,"E4.bottom");var subQ2=sQuery(id+"F0.wireOp",EDGE,"E0.right");var subQ3=sQuery(id+"F0.wireOp",EDGE,"E0.bottom");Q11=makeQuery(id+"F27.boolean.opBoolean","MERGE",EDGE,{"derivedFrom":[makeQuery(id+"F11.opExtrude","CAP_EDGE",EDGE,{"disambiguationData":[OSD([subQ3,subQ2,subQ1,subQ0])],"isStart":false}),makeQuery(id+"F27.opExtrude","SWEPT_EDGE",EDGE,{"disambiguationData":[OSD([subQ3,sQuery(id+"F0.wireOp",EDGE,"E0.top"),sQuery(id+"F0.wireOp",EDGE,"E0.left"),subQ2,sQuery(id+"F2.wireOp",EDGE,"E1.top"),sQuery(id+"F2.wireOp",EDGE,"E1.right"),sQuery(id+"F6.wireOp",EDGE,"E3"),subQ1,subQ0,sQuery(id+"F10.wireOp",EDGE,"E5"),sQuery(id+"F12.wireOp",EDGE,"E6.bottom"),sQuery(id+"F12.wireOp",EDGE,"E6.left")])]})]});}
            var Q12;
            Q12=makeQuery(id+"F23.boolean.opBoolean","COPY",EDGE,{"derivedFrom":makeQuery(id+"F23.opExtrude","CAP_EDGE",EDGE,{"disambiguationData":[OSD([sQuery(id+"F22.wireOp",EDGE,"E13")])],"isStart":true})});
            fillet(context, id + "F30", {"entities" : qUnion([Q0, Q1, Q2, Q3, Q4, Q5, Q6, Q7, Q8, Q9, Q10, Q11, Q12]), "radius" : 5 * mm, "tangentPropagation" : true, "allowEdgeOverflow" : false});
        }
    });
